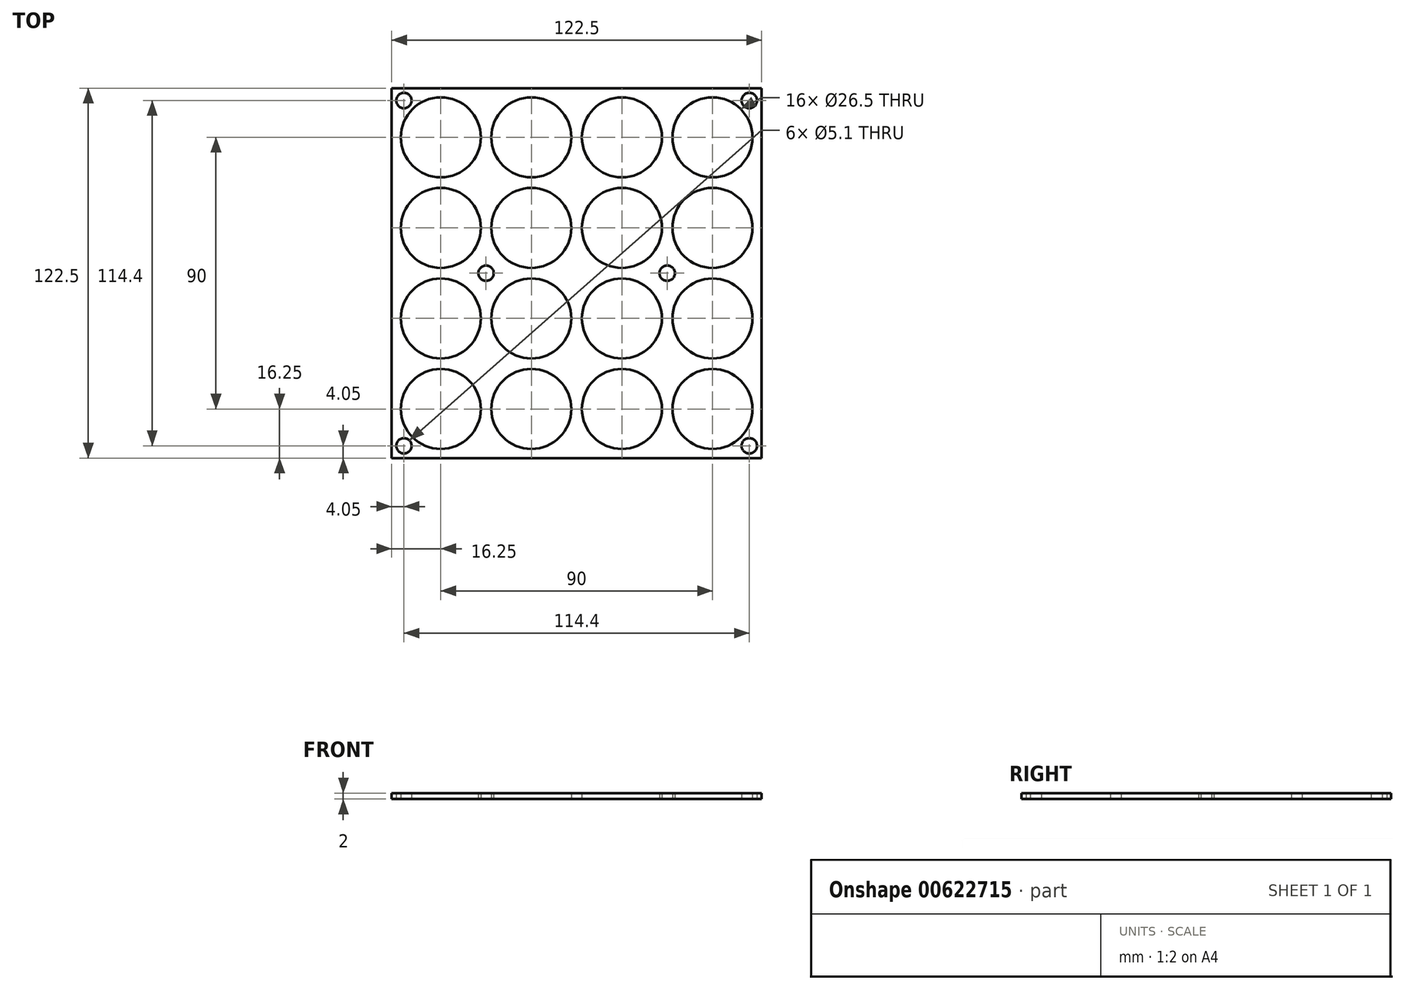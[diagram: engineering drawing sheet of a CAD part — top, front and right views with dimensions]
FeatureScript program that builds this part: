
annotation { "Feature Type Name" : "Feature", "Feature Type Description" : "" }
export const myFeature = defineFeature(function(context is Context, id is Id, definition is map)
    precondition{}
    {
        {
            var Q0;
            Q0=qCreatedBy(makeId("Top.planeOp"),FACE);
            var sketch = newSketch(context, id + "F0", { "sketchPlane" : qUnion([Q0])});
            skLineSegment(sketch, "E0.bottom", {"start": v(-61.25, 61.25) * mm, "end": v(61.25, 61.25) * mm});
            skLineSegment(sketch, "E0.top", {"start": v(-61.25, -61.25) * mm, "end": v(61.25, -61.25) * mm});
            skLineSegment(sketch, "E0.left", {"start": v(-61.25, 61.25) * mm, "end": v(-61.25, -61.25) * mm});
            skLineSegment(sketch, "E0.right", {"start": v(61.25, 61.25) * mm, "end": v(61.25, -61.25) * mm});
            skPoint(sketch, "E0.middle", {"position": v(0, 0) * mm});
            skCircle(sketch, "E1", {"center": v(-45, 45) * mm, "radius": 13.25 * mm});
            skCircle(sketch, "E2.0.1.0", {"center": v(-45, 15) * mm, "radius": 13.25 * mm});
            skCircle(sketch, "E2.0.2.0", {"center": v(-45, -15) * mm, "radius": 13.25 * mm});
            skCircle(sketch, "E2.0.3.0", {"center": v(-45, -45) * mm, "radius": 13.25 * mm});
            skCircle(sketch, "E2.1.0.0", {"center": v(-15, 45) * mm, "radius": 13.25 * mm});
            skCircle(sketch, "E2.1.1.0", {"center": v(-15, 15) * mm, "radius": 13.25 * mm});
            skCircle(sketch, "E2.1.2.0", {"center": v(-15, -15) * mm, "radius": 13.25 * mm});
            skCircle(sketch, "E2.1.3.0", {"center": v(-15, -45) * mm, "radius": 13.25 * mm});
            skCircle(sketch, "E2.2.0.0", {"center": v(15, 45) * mm, "radius": 13.25 * mm});
            skCircle(sketch, "E2.2.1.0", {"center": v(15, 15) * mm, "radius": 13.25 * mm});
            skCircle(sketch, "E2.2.2.0", {"center": v(15, -15) * mm, "radius": 13.25 * mm});
            skCircle(sketch, "E2.2.3.0", {"center": v(15, -45) * mm, "radius": 13.25 * mm});
            skCircle(sketch, "E2.3.0.0", {"center": v(45, 45) * mm, "radius": 13.25 * mm});
            skCircle(sketch, "E2.3.1.0", {"center": v(45, 15) * mm, "radius": 13.25 * mm});
            skCircle(sketch, "E2.3.2.0", {"center": v(45, -15) * mm, "radius": 13.25 * mm});
            skCircle(sketch, "E2.3.3.0", {"center": v(45, -45) * mm, "radius": 13.25 * mm});
            skLineSegment(sketch, "E2.direction1", {"start": v(-45, 45) * mm, "end": v(-15, 45) * mm, "construction": true});
            skLineSegment(sketch, "E2.direction2", {"start": v(-45, 45) * mm, "end": v(-45, 15) * mm, "construction": true});
            skLineSegment(sketch, "E3", {"start": v(0, 88.74) * mm, "end": v(0, -97.9) * mm, "construction": true});
            skLineSegment(sketch, "E4", {"start": v(-96.24, 0) * mm, "end": v(100.37, 0) * mm, "construction": true});
            skCircle(sketch, "E5", {"center": v(-30, 0) * mm, "radius": 2.55 * mm});
            skCircle(sketch, "E6", {"center": v(-57.2, 57.2) * mm, "radius": 2.55 * mm});
            skCircle(sketch, "E7.MirrorC", {"center": v(30, 0) * mm, "radius": 2.55 * mm});
            skCircle(sketch, "E8.MirrorC", {"center": v(57.2, 57.2) * mm, "radius": 2.55 * mm});
            skCircle(sketch, "E9.MirrorC", {"center": v(-57.2, -57.2) * mm, "radius": 2.55 * mm});
            skCircle(sketch, "E10.MirrorC", {"center": v(57.2, -57.2) * mm, "radius": 2.55 * mm});
            skSolve(sketch);
        }
        {
            var Q0;
            Q0=makeQuery(id+"F0.imprint","IMPRINT",FACE,{"disambiguationData":[TD([[makeQuery(id+"F0.imprint","IMPRINT",EDGE,{"derivedFrom":sQuery(id+"F0.wireOp",EDGE,"E0.bottom")}),-1.0]])]});
            extrude(context, id + "F1", {"entities" : qUnion([Q0]), "depth" : 2 * mm, "offsetDistance" : 25 * mm});
        }
    });
